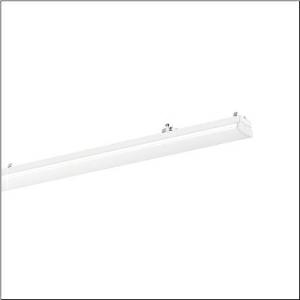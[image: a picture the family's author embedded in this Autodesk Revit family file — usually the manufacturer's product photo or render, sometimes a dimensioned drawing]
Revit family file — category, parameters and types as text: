
# Revit family: licross_r__21_recessed_opal_mo_52tl1ddn425g_d02a
name_source: partatom
category: Lighting Fixtures
units: mm (PartAtom-declared; Revit-internal decimal feet)

## family parameters
Cut with Voids When Loaded = No
Host = Face
Light Source = No
Part Type = Normal
Room Calculation Point = No
Round Connector Dimension = Use Diameter
Shared = No

## types (1)
- --- (1 x LED, 2750 lm, 16.2 W, 4000K)
    Apparent Load = 16 VA
    CIE Flux Codes = 44 73 91 87 100
    Color Rendering = 80
    Color Temperature = 4000K
    Default Elevation = 1800 mm
    Description = Licross® 21 recessed opal MO, luminaire insert, of sheet steel, galvanised, coil coated, white, length: 1.500mm, width: 66mm, height: 67mm, LED rated luminous flux: 2.750lm, light colour: 840, control gear: DALI 2, with plug, 5-pole, with phase selection, mains connection: 220..240V, AC, 50/60Hz, rated input power: 16W, internal wiring halogen-free, primary optical cover: cover, of PMMA, light emission: direct with ceiling illumination distribution, primary light characteristic: symmetric, protection rating (complete): IP40, insulation class (complete): insulation class I (protective earthing), certification: CE, ENEC, VDE, UKCA, protection symbol: D if used in an environment without relevant dust loads with corresponding accessories, impact resistance: IK06, permissible ambient temperature for indoor applications: -25..+50°C, corresponds to IFS (International Featured Standards) requirements for safety and quality in the food industry, reducing of maximum allowable ambient temperature of 5°C with ceiling mounting, LABS conformity tested according to VDMA 24364:2018-05, packaging unit: 1 piece
    Height = 83 mm
    Lamp = 1 x LED
    Lamp Light Flux = 2750 lm
    Lamp Power = 16.2 W
    Lamp count = 1
    Length = 1500 mm
    Luminous efficacy = 170 lm/W
    Manufacturer = Siteco
    ModVariant = No
    Model = 52TL1DDN425G
    Mounting Place = Ceiling
    Mounting Type = Pendant
    Number of Poles = 1
    OnlyDefault = Yes
    Power Factor = 1
    Product Name = Licross® 21 recessed opal MO
    Product group = luminaire insert | ceiling pendant
    ProductGroupID = 902
    Protection Class = Protection class I
    Protection Degree = IP 40
    RLX_Detail_Level = 1
    RLX_Emergency_Light_Flux = 0 lm
    RLX_Emergency_Type = 0
    RLX_Emergency_Type_DB = No
    RlxData = <blob elided: 25869 chars, md5=f28d9e03>
    Socket = socket
    Standby Power = 0 W
    System Light Flux = 2750 lm
    System Power = 16 W
    Type Comments = factory setting: luminous flux: 100 % | dim-lin: 254 | 104 mA
    Type Image = l_1313666.jpg
    URL = http://relux.com
    VarID = @adj_084561
    Voltage = 0 V
    Weight = 0.00 kg
    Width = 76 mm

## geometry (parser evidence)
native form markers: Blend x4, Sweep x12
no freeform markers — native parametric forms only
